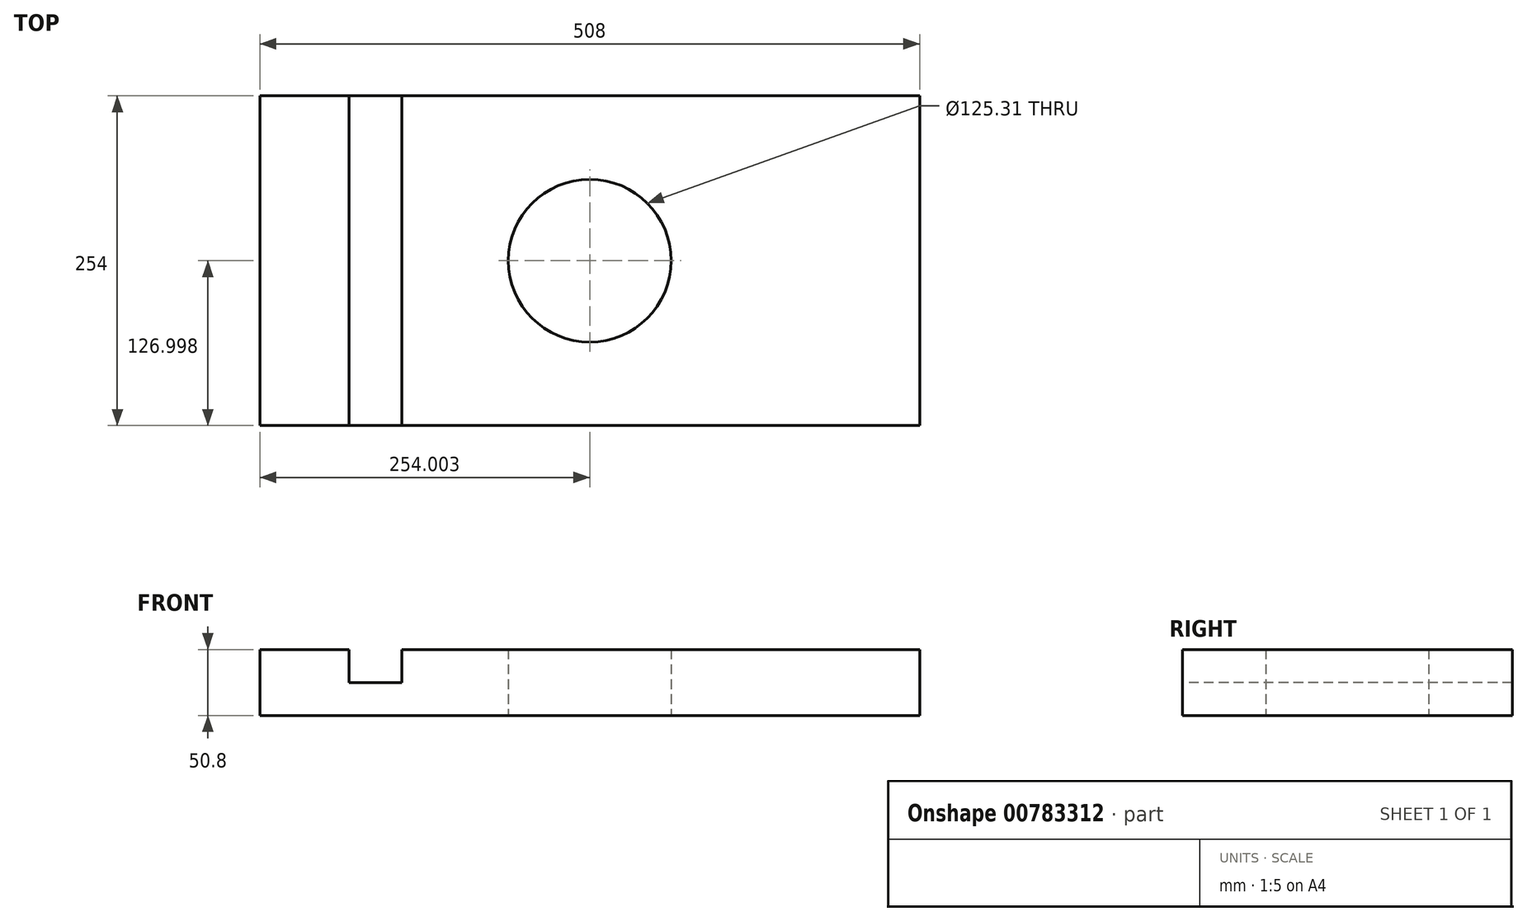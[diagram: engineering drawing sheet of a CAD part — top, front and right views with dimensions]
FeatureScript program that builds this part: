
annotation { "Feature Type Name" : "Feature", "Feature Type Description" : "" }
export const myFeature = defineFeature(function(context is Context, id is Id, definition is map)
    precondition{}
    {
        {
            var Q0;
            Q0=qCreatedBy(makeId("Top.planeOp"),FACE);
            var sketch = newSketch(context, id + "F0", { "sketchPlane" : qUnion([Q0])});
            skLineSegment(sketch, "E0.bottom", {"start": v(362.64, -13.45) * mm, "end": v(-145.36, -13.45) * mm});
            skLineSegment(sketch, "E0.top", {"start": v(362.64, 240.55) * mm, "end": v(-145.36, 240.55) * mm});
            skLineSegment(sketch, "E0.left", {"start": v(362.64, -13.45) * mm, "end": v(362.64, 240.55) * mm});
            skLineSegment(sketch, "E0.right", {"start": v(-145.36, -13.45) * mm, "end": v(-145.36, 240.55) * mm});
            skPoint(sketch, "E0.middle", {"position": v(108.64, 113.55) * mm});
            skPoint(sketch, "E1.middle", {"position": v(362.64, 240.55) * mm});
            skCircle(sketch, "E2", {"center": v(108.64, 113.55) * mm, "radius": 62.65 * mm});
            skSolve(sketch);
        }
        {
            var Q0;
            Q0=makeQuery(id+"F0.imprint","IMPRINT",FACE,{"disambiguationData":[TD([[makeQuery(id+"F0.imprint","IMPRINT",EDGE,{"derivedFrom":sQuery(id+"F0.wireOp",EDGE,"E0.bottom")}),-1.0]])]});
            extrude(context, id + "F1", {"entities" : qUnion([Q0]), "depth" : 25.4 * mm, "offsetDistance" : 25.4 * mm});
        }
        {
            var Q0;
            Q0=makeQuery(id+"F1.opExtrude","CAP_FACE",FACE,{"disambiguationData":[OSD([sQuery(id+"F0.wireOp",EDGE,"E0.bottom"),sQuery(id+"F0.wireOp",EDGE,"E0.top"),sQuery(id+"F0.wireOp",EDGE,"E0.left"),sQuery(id+"F0.wireOp",EDGE,"E0.right"),sQuery(id+"F0.wireOp",EDGE,"E2")])],"isStart":false});
            extrude(context, id + "F2", {"entities" : qUnion([Q0]), "operationType" : NewBodyOperationType.ADD, "depth" : 25.4 * mm, "offsetDistance" : 25.4 * mm});
        }
        {
            var Q0;
            Q0=makeQuery(id+"F2.opExtrude","CAP_FACE",FACE,{"disambiguationData":[OSD([sQuery(id+"F0.wireOp",EDGE,"E0.bottom"),sQuery(id+"F0.wireOp",EDGE,"E0.top"),sQuery(id+"F0.wireOp",EDGE,"E0.left"),sQuery(id+"F0.wireOp",EDGE,"E0.right"),sQuery(id+"F0.wireOp",EDGE,"E2")])],"isStart":false});
            var sketch = newSketch(context, id + "F3", { "sketchPlane" : qUnion([Q0])});
            skLineSegment(sketch, "E3.bottom", {"start": v(89.95, 240.55) * mm, "end": v(85.33, 240.55) * mm});
            skLineSegment(sketch, "E4.bottom", {"start": v(-76.53, 240.55) * mm, "end": v(-36.07, 240.55) * mm});
            skLineSegment(sketch, "E4.top", {"start": v(-76.53, -13.45) * mm, "end": v(-36.07, -13.45) * mm});
            skLineSegment(sketch, "E4.left", {"start": v(-76.53, 240.55) * mm, "end": v(-76.53, -13.45) * mm});
            skLineSegment(sketch, "E4.right", {"start": v(-36.07, 240.55) * mm, "end": v(-36.07, -13.45) * mm});
            skSolve(sketch);
        }
        {
            var Q0;
            Q0=makeQuery(id+"F3.imprint","IMPRINT",FACE,{"disambiguationData":[TD([[makeQuery(id+"F3.imprint","IMPRINT",EDGE,{"derivedFrom":sQuery(id+"F3.wireOp",EDGE,"E4.bottom")}),1.0]])]});
            extrude(context, id + "F4", {"entities" : qUnion([Q0]), "operationType" : NewBodyOperationType.REMOVE, "oppositeDirection" : true, "depth" : 25.4 * mm, "offsetDistance" : 25.4 * mm});
        }
    });
